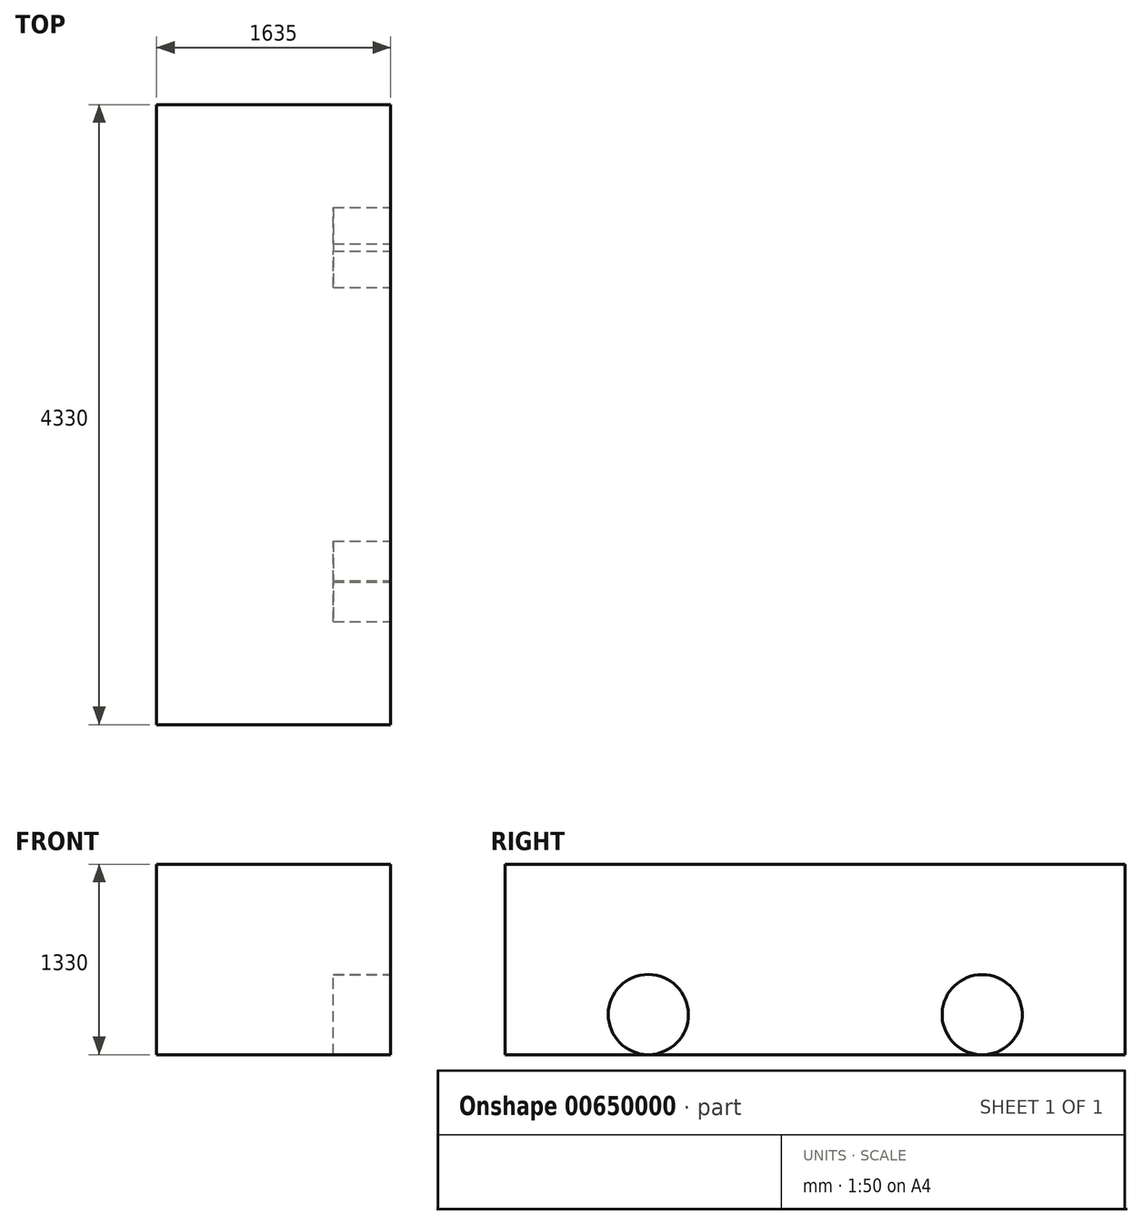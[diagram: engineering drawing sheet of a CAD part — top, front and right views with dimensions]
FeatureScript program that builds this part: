
annotation { "Feature Type Name" : "Feature", "Feature Type Description" : "" }
export const myFeature = defineFeature(function(context is Context, id is Id, definition is map)
    precondition{}
    {
        {
            var Q0;
            Q0=qCreatedBy(makeId("Right.planeOp"),FACE);
            var sketch = newSketch(context, id + "F0", { "sketchPlane" : qUnion([Q0])});
            skLineSegment(sketch, "E0.bottom", {"start": v(2165, 665) * mm, "end": v(-2165, 665) * mm});
            skLineSegment(sketch, "E0.top", {"start": v(2165, -665) * mm, "end": v(-2165, -665) * mm});
            skLineSegment(sketch, "E0.left", {"start": v(2165, 665) * mm, "end": v(2165, -665) * mm});
            skLineSegment(sketch, "E0.right", {"start": v(-2165, 665) * mm, "end": v(-2165, -665) * mm});
            skPoint(sketch, "E0.middle", {"position": v(0, 0) * mm});
            skSolve(sketch);
        }
        {
            var Q0;
            Q0=makeQuery(id+"F0.imprint","IMPRINT",FACE,{"disambiguationData":[TD([[makeQuery(id+"F0.imprint","IMPRINT",EDGE,{"derivedFrom":sQuery(id+"F0.wireOp",EDGE,"E0.bottom")}),1.0]])]});
            extrude(context, id + "F1", {"entities" : qUnion([Q0]), "depth" : 817.5 * mm, "offsetDistance" : 25 * mm, "hasSecondDirection" : true, "secondDirectionOppositeDirection" : true, "secondDirectionDepth" : 817.5 * mm});
        }
        {
            var Q0;
            Q0=makeQuery(id+"F1.opExtrude","CAP_FACE",FACE,{"disambiguationData":[OSD([sQuery(id+"F0.wireOp",EDGE,"E0.bottom"),sQuery(id+"F0.wireOp",EDGE,"E0.top"),sQuery(id+"F0.wireOp",EDGE,"E0.left"),sQuery(id+"F0.wireOp",EDGE,"E0.right")])],"isStart":false});
            var sketch = newSketch(context, id + "F2", { "sketchPlane" : qUnion([Q0])});
            skCircle(sketch, "E1", {"center": v(-1165, -385.03) * mm, "radius": 280 * mm});
            skPoint(sketch, "E1.first.point", {"position": v(-1168.98, -665) * mm});
            skPoint(sketch, "E1.second.point", {"position": v(-1239.79, -115.2) * mm});
            skPoint(sketch, "E1.third.point", {"position": v(-900.49, -293.2) * mm});
            skArc(sketch, "E2", {"start": v(-1693.12, -665) * mm, "mid": v(-1507.65, -554.67) * mm, "end": v(-1442.66, -348.88) * mm});
            skArc(sketch, "E3", {"start": v(-885.04, -380.54) * mm, "mid": v(-772.05, -622) * mm, "end": v(-508.96, -665) * mm});
            skSolve(sketch);
        }
        {
            var Q0;
            Q0=makeQuery(id+"F1.opExtrude","CAP_FACE",FACE,{"disambiguationData":[OSD([sQuery(id+"F0.wireOp",EDGE,"E0.bottom"),sQuery(id+"F0.wireOp",EDGE,"E0.top"),sQuery(id+"F0.wireOp",EDGE,"E0.left"),sQuery(id+"F0.wireOp",EDGE,"E0.right")])],"isStart":false});
            var sketch = newSketch(context, id + "F3", { "sketchPlane" : qUnion([Q0])});
            skPoint(sketch, "E4", {"position": v(1165, -385) * mm});
            skPoint(sketch, "E5", {"position": v(1165, -665) * mm});
            skPoint(sketch, "E6", {"position": v(2165, -385) * mm});
            skSolve(sketch);
        }
        {
            var Q0;
            Q0=makeQuery(id+"F3.imprint","IMPRINT",FACE,{"disambiguationData":[TD([[makeQuery(id+"F3.imprint","IMPRINT",EDGE,{"derivedFrom":makeQuery(id+"F1.opExtrude","CAP_EDGE",EDGE,{"disambiguationData":[OSD([sQuery(id+"F0.wireOp",EDGE,"E0.bottom")])],"isStart":false})}),1.0]])]});
            var sketch = newSketch(context, id + "F4", { "sketchPlane" : qUnion([Q0])});
            skCircle(sketch, "E7", {"center": v(1167.06, -386.13) * mm, "radius": 280 * mm});
            skSolve(sketch);
        }
        {
            var Q0;
            Q0 = qSketchRegion(id + "F2", true);
            extrude(context, id + "F5", {"entities" : qUnion([Q0]), "operationType" : NewBodyOperationType.REMOVE, "oppositeDirection" : true, "depth" : 400 * mm, "offsetDistance" : 25 * mm});
        }
        {
            var Q0;
            Q0 = qSketchRegion(id + "F4", true);
            extrude(context, id + "F6", {"entities" : qUnion([Q0]), "operationType" : NewBodyOperationType.REMOVE, "oppositeDirection" : true, "depth" : 400 * mm, "offsetDistance" : 25 * mm});
        }
    });
